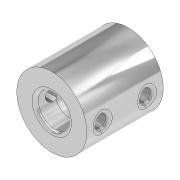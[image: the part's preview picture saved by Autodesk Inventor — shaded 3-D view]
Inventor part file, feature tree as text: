
AUTODESK INVENTOR PART (.ipt)
format: ipt  version: 2020 (Build 240168000, 168)  size: 232,448 bytes
history: native  units: in
note: dims shown in document units (in); Inventor stores cm internally (conversion verified against a paired STEP export)
features: extrude x2, chamfer x2, sketch x2, fillet x1
ambient origin geometry x8: Origin, YZ Plane, XZ Plane, XY Plane, X Axis, Y Axis, Z Axis, Center Point
bodies: Solid1 (feature_tree)
feature tree (7):
  extrude  "Extrusion1"  Depth=0.315in
  extrude  "Extrusion2"  Depth=0.1969in
  chamfer  "Chamfer1"  Distance=0.1969in
  chamfer  "Chamfer2"  Distance=0.0787in
  fillet  "Fillet1"  Radius=0.0787in
  sketch  "Sketch1"  dims[d0=0.1969in d1=0.315in]
  sketch  "Sketch2"  dims[d2=0.4724in d3=0.0in d4=0.1969in d5=0.1969in d6=0.0787in d7=0.0787in d8=0.4724in d9=0.0in d10=0.1181in d11=0.125in d12=0.0137in d13=0.1181in d14=0.125in d15=0.0137in d16=0.0197in d17=0.1181in]
